# Revit family: Sirena evacuacion por voz_Aguilera Electronica
name_source: partatom
category: Dispositivos de alarma de incendios
revit_build: Autodesk Revit 2017 (Build: 20160225_1515(x64)
units: mm (PartAtom-declared; Revit-internal decimal feet)

## family parameters
Anfitrión = Cara
Compartido = No
Corte con vacíos al cargar = No
Cota de conector redondo = Diámetro de uso
Mantener orientación de anotación = Sí
Número OmniClass = 23.85.30.21.14.11
Punto de cálculo de habitación = No
Tipo de pieza = Normal
Título OmniClass = Concentration Detection Bells and Sounders

## types (1)
- Sirena de evacuación por voz
    Altura 1 = 10 mm  [stored 0.0328084 ft]
    Altura 2 = 53 mm  [stored 0.173885 ft]
    Altura 3 = 17 mm
    Altura 4 = 30 mm  [stored 0.0984252 ft]
    Comentarios de tipo = Sirena de elevada potencia acústica con foco de LEDs para uso interior. Incluye etiquetas: INCENDIO, FUEGO, FIRE, FOGO

Certificada según EN 54-3
Tensión de trabajo 24Vcc
Consumo máximo: 60mA
Nivel sonoro: 95dB / 1m
Protección: IP30
Dimensiones: 110x190x55mm
    Descripción = Sirenas de alarma por voz de bajo consumo. Estas sirenas disponen de seis mensajes grabados en español.
Se recomienda el uso de las sirenas de alarma por voz en aquellas aplicaciones donde se quieran evitar confusiones en el público. Este tipo de sirenas identifica de una manera concisa la acción a llevar a cabo en caso de emergencia, hecho de vital importancia en edificios públicos y comerciales, donde los ocupantes normalmente no están familiarizados en los protocolos de evacuación.
Dos modelos disponibles:
AE/V-ASV Sirena con voz
Tienen 6 mensajes de evacuación en español grabados, válidos para un aviso de incendio, evacuación general, descarga de gas de extinción o evacuación de un parking por alta concentración de monóxido:
1) 015 - ¡Esta es una alarma de incendio! Por favor, abandonen el edificio inmediatamente.
2) 014 - ¡Atención! ¡Atención! Esto es una emergencia, Por favor abandonen el edificio por la salida más próxima.
3) 066 - ¡Por favor abandone la zona inmediatamente!. Descarga de gas inminente.
4) 001 - Atención por favor, Atención por favor. Se ha detectado una alarma de incendio en el edificio. Por favor, abandonen el edificio inmediatamente por la salida más próxima.
5) 064 - Liberación inminente de gas de extinción. Evacue el área inmediatamente.
6) 071 - Se ha detectado un nivel peligroso de monóxido de carbono, por favor abandonen el área inmediatamente
.
    Diámetro tubo = 20 mm  [stored 0.0656168 ft]
    Elevación por defecto = 1200 mm
    Fabricante = Aguilera Electrónica
    Modelo = Referencia: AE/V-ASV
    Símbolo = Sí
    Símbolo texto modelo = Sí
    URL = https://aguilera.es

note: [stored X ft] marks values corroborated as IEEE doubles in the binary element streams (Revit-internal decimal feet)
